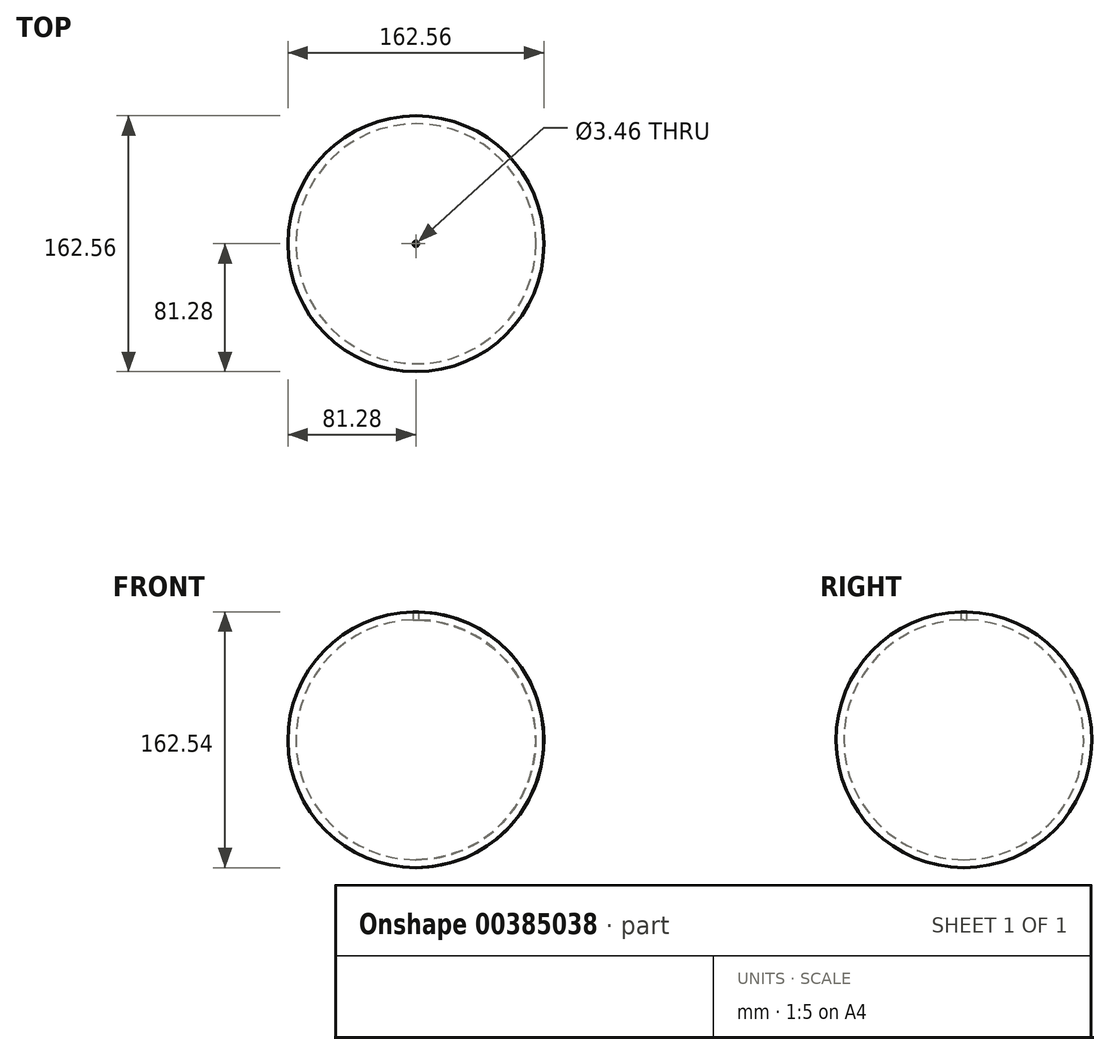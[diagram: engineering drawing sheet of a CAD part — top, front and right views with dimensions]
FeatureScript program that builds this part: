
annotation { "Feature Type Name" : "Feature", "Feature Type Description" : "" }
export const myFeature = defineFeature(function(context is Context, id is Id, definition is map)
    precondition{}
    {
        {
            var Q0;
            Q0=qCreatedBy(makeId("Front.planeOp"),FACE);
            var sketch = newSketch(context, id + "F0", { "sketchPlane" : qUnion([Q0])});
            skArc(sketch, "E0", {"start": v(0, -81.28) * mm, "mid": v(81.28, -0.87) * mm, "end": v(1.73, 81.26) * mm});
            skArc(sketch, "E1", {"start": v(0, -76.2) * mm, "mid": v(76.2, -0.87) * mm, "end": v(1.73, 76.18) * mm});
            skLineSegment(sketch, "E2", {"start": v(0, -81.28) * mm, "end": v(0, 85.2) * mm, "construction": true});
            skLineSegment(sketch, "E3.MirrorCS", {"start": v(1.73, 81.26) * mm, "end": v(1.73, 76.18) * mm});
            skPoint(sketch, "E4.orphan", {"position": v(0, 76.2) * mm});
            skLineSegment(sketch, "E5", {"start": v(0, -76.2) * mm, "end": v(0, -81.28) * mm});
            skSolve(sketch);
        }
        {
            var Q0;
            Q0 = qSketchRegion(id + "F0", true);
            var Q1;
            Q1=sQuery(id+"F0.wireOp",EDGE,"E2");
            revolve(context, id + "F1", {"entities" : qUnion([Q0]), "axis" : qUnion([Q1]), "revolveType" : RevolveType.FULL});
        }
    });
